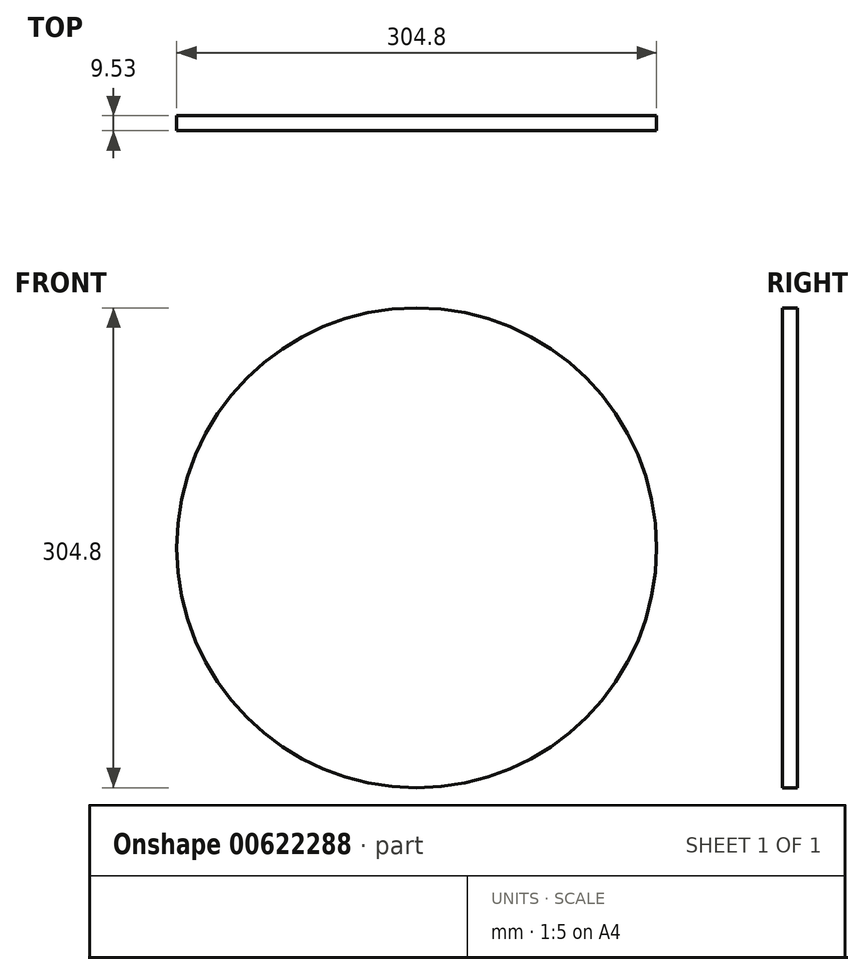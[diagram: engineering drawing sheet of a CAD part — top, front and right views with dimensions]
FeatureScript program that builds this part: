
annotation { "Feature Type Name" : "Feature", "Feature Type Description" : "" }
export const myFeature = defineFeature(function(context is Context, id is Id, definition is map)
    precondition{}
    {
        {
            var Q0;
            Q0=qCreatedBy(makeId("Front.planeOp"),FACE);
            var sketch = newSketch(context, id + "F0", { "sketchPlane" : qUnion([Q0])});
            skCircle(sketch, "E0", {"center": v(0, 0) * mm, "radius": 152.4 * mm});
            skSolve(sketch);
        }
        {
            var Q0;
            Q0=makeQuery(id+"F0.imprint","IMPRINT",FACE,{"disambiguationData":[TD([[makeQuery(id+"F0.imprint","IMPRINT",EDGE,{"derivedFrom":sQuery(id+"F0.wireOp",EDGE,"E0")}),1.0]])]});
            extrude(context, id + "F1", {"entities" : qUnion([Q0]), "depth" : 9.52 * mm, "offsetDistance" : 25.4 * mm});
        }
    });
